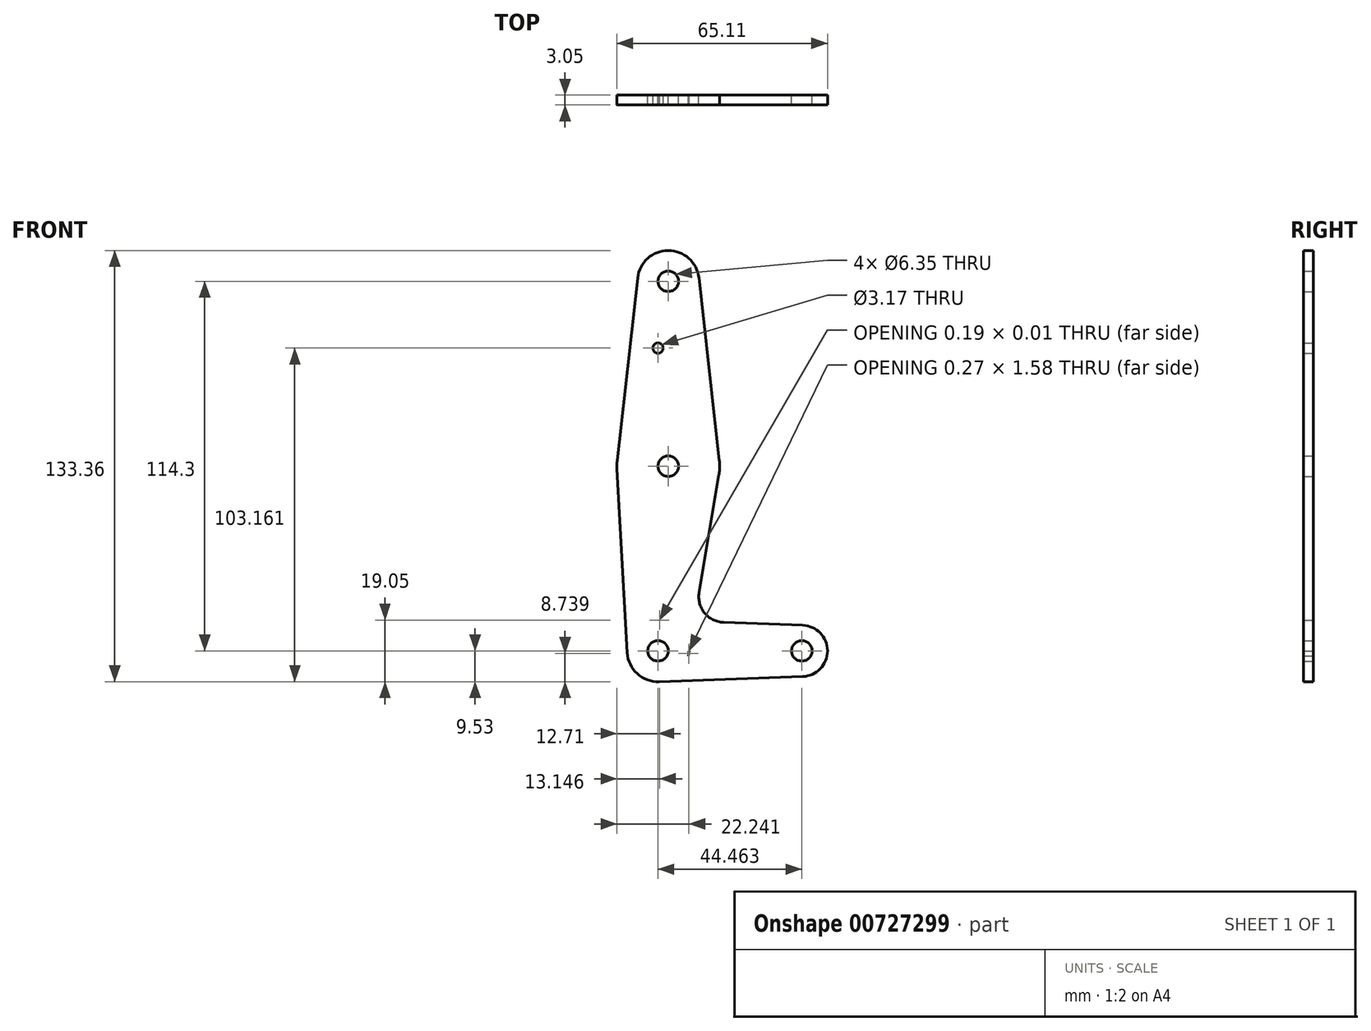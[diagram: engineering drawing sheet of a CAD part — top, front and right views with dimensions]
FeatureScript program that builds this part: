
annotation { "Feature Type Name" : "Feature", "Feature Type Description" : "" }
export const myFeature = defineFeature(function(context is Context, id is Id, definition is map)
    precondition{}
    {
        {
            var Q0;
            Q0=qCreatedBy(makeId("Front.planeOp"),FACE);
            var sketch = newSketch(context, id + "F0", { "sketchPlane" : qUnion([Q0])});
            skLineSegment(sketch, "E0", {"start": v(0, 0) * mm, "end": v(44.46, 0) * mm});
            skLineSegment(sketch, "E1", {"start": v(0, 0) * mm, "end": v(3.18, 57.1) * mm});
            skArc(sketch, "E2", {"start": v(18.84, 54.47) * mm, "mid": v(19.05, 56.67) * mm, "end": v(18.96, 58.87) * mm});
            skLineSegment(sketch, "E3", {"start": v(3.18, 57.1) * mm, "end": v(3.18, 114.3) * mm});
            skArc(sketch, "E4", {"start": v(12.64, 115.36) * mm, "mid": v(3.18, 123.83) * mm, "end": v(-6.3, 115.36) * mm});
            skArc(sketch, "E5", {"start": v(0.53, 9.52) * mm, "mid": v(0.44, 9.52) * mm, "end": v(0.34, 9.52) * mm});
            skArc(sketch, "E6", {"start": v(44.75, -7.93) * mm, "mid": v(52.4, 0) * mm, "end": v(44.75, 7.93) * mm});
            skLineSegment(sketch, "E7", {"start": v(-12.6, 58.87) * mm, "end": v(-6.3, 115.36) * mm});
            skLineSegment(sketch, "E8", {"start": v(-12.68, 56.22) * mm, "end": v(-9.52, -0.53) * mm});
            skLineSegment(sketch, "E9", {"start": v(0.34, -9.52) * mm, "end": v(44.75, -7.93) * mm});
            skLineSegment(sketch, "E10", {"start": v(0.34, 9.52) * mm, "end": v(0.53, 9.52) * mm});
            skLineSegment(sketch, "E11", {"start": v(18.84, 54.47) * mm, "end": v(12.7, 18.07) * mm});
            skLineSegment(sketch, "E12", {"start": v(12.64, 115.36) * mm, "end": v(18.96, 58.87) * mm});
            skLineSegment(sketch, "E13.trimOffspring", {"start": v(20.26, 8.8) * mm, "end": v(44.75, 7.93) * mm});
            skLineSegment(sketch, "E14.trimOffspring", {"start": v(9.66, 0) * mm, "end": v(9.4, -1.58) * mm});
            skArc(sketch, "E15.trimOffspring", {"start": v(-9.52, -0.53) * mm, "mid": v(-6.42, -7.04) * mm, "end": v(0.34, -9.52) * mm});
            skArc(sketch, "E16.trimOffspring", {"start": v(9.4, -1.58) * mm, "mid": v(9.5, -0.8) * mm, "end": v(9.53, 0) * mm});
            skArc(sketch, "E17.trimOffspring", {"start": v(-12.6, 58.87) * mm, "mid": v(-12.7, 57.55) * mm, "end": v(-12.68, 56.22) * mm});
            skPoint(sketch, "E18.visualSharp", {"position": v(11.2, 9.13) * mm});
            skArc(sketch, "E18.filletArc", {"start": v(12.7, 18.07) * mm, "mid": v(14.39, 11.73) * mm, "end": v(20.26, 8.8) * mm});
            skCircle(sketch, "E19", {"center": v(0, 93.63) * mm, "radius": 1.59 * mm});
            skCircle(sketch, "E20", {"center": v(3.18, 114.3) * mm, "radius": 3.18 * mm});
            skCircle(sketch, "E21", {"center": v(3.18, 57.1) * mm, "radius": 3.18 * mm});
            skCircle(sketch, "E22", {"center": v(0, 0) * mm, "radius": 3.18 * mm});
            skCircle(sketch, "E23", {"center": v(44.46, 0) * mm, "radius": 3.18 * mm});
            skSolve(sketch);
        }
        {
            var Q0;
            Q0 = qSketchRegion(id + "F0", true);
            extrude(context, id + "F1", {"entities" : qUnion([Q0]), "depth" : 3.05 * mm, "offsetDistance" : 25.4 * mm});
        }
    });
